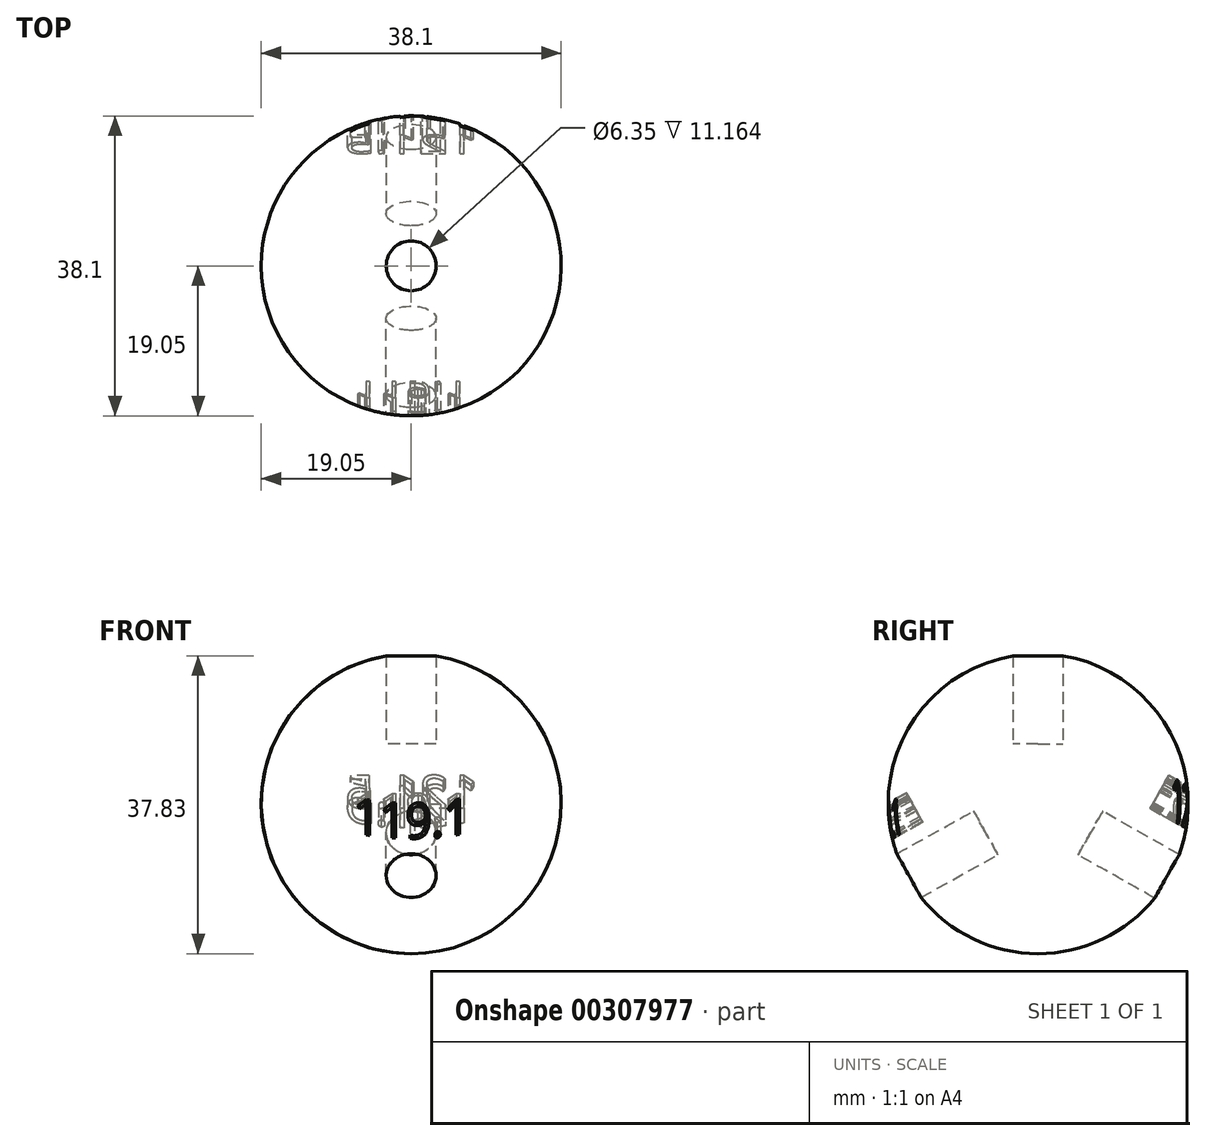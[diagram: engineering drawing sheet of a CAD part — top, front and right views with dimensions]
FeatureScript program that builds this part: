
annotation { "Feature Type Name" : "Feature", "Feature Type Description" : "" }
export const myFeature = defineFeature(function(context is Context, id is Id, definition is map)
    precondition{}
    {
        {
            var Q0;
            Q0=qCreatedBy(makeId("Front.planeOp"),FACE);
            var sketch = newSketch(context, id + "F0", { "sketchPlane" : qUnion([Q0])});
            skArc(sketch, "E0", {"start": v(0, 19.05) * mm, "mid": v(-19.05, 0) * mm, "end": v(0, -19.05) * mm});
            skLineSegment(sketch, "E1", {"start": v(0, 19.05) * mm, "end": v(0, -19.05) * mm});
            skSolve(sketch);
        }
        {
            var Q0;
            Q0=qCreatedBy(makeId("Top.planeOp"),FACE);
            var sketch = newSketch(context, id + "F1", { "sketchPlane" : qUnion([Q0])});
            skCircle(sketch, "E2", {"center": v(0, 0) * mm, "radius": 19.05 * mm});
            skSolve(sketch);
        }
        {
            var Q0;
            Q0=makeQuery(id+"F0.imprint","IMPRINT",FACE,{"disambiguationData":[TD([[makeQuery(id+"F0.imprint","IMPRINT",EDGE,{"derivedFrom":sQuery(id+"F0.wireOp",EDGE,"E0")}),1.0]])]});
            var Q1;
            Q1=sQuery(id+"F1.wireOp",EDGE,"E2");
            revolve(context, id + "F2", {"entities" : qUnion([Q0]), "axis" : qUnion([Q1]), "revolveType" : RevolveType.FULL});
        }
        {
            var Q0;
            Q0=qCreatedBy(makeId("Front.planeOp"),FACE);
            var sketch = newSketch(context, id + "F3", { "sketchPlane" : qUnion([Q0])});
            skLineSegment(sketch, "E3", {"start": v(0, 0) * mm, "end": v(76.32, 0) * mm, "construction": true});
            skLineSegment(sketch, "E4", {"start": v(0, 0) * mm, "end": v(0, 76.7) * mm, "construction": true});
            skSolve(sketch);
        }
        {
            var Q0;
            Q0=qCreatedBy(makeId("Top.planeOp"),FACE);
            cPlane(context, id + "F4", {"entities" : qUnion([Q0]), "cplaneType" : CPlaneType.OFFSET, "offset" : 7.62 * mm, "width" : 152.4 * mm, "height" : 152.4 * mm});
        }
        {
            var Q0;
            Q0=qCreatedBy(id+"F4.planeOp",FACE);
            var sketch = newSketch(context, id + "F5", { "sketchPlane" : qUnion([Q0])});
            skCircle(sketch, "E5", {"center": v(0, 0) * mm, "radius": 3.17 * mm});
            skSolve(sketch);
        }
        {
            var Q0;
            Q0=qSketchRegion(id+"F5",true);
            extrude(context, id + "F6", {"entities" : qUnion([Q0]), "depth" : 76.2 * mm});
        }
        {
            var Q0;
            Q0=makeQuery(id+"F6.opExtrude","SWEPT_BODY",BODY,{"disambiguationData":[OSD([sQuery(id+"F5.wireOp",EDGE,"E5")])]});
            var Q1;
            Q1=sQuery(id+"F3.wireOp",EDGE,"E3");
            transform(context, id + "F7", {"entities" : qUnion([Q0]), "transformType" : TransformType.ROTATION, "transformAxis" : qUnion([Q1]), "angle" : 119.1 * degree, "makeCopy" : true});
        }
        {
            var Q0;
            Q0=makeQuery(id+"F7.opPattern","COPY",BODY,{"derivedFrom":makeQuery(id+"F6.opExtrude","SWEPT_BODY",BODY,{"disambiguationData":[OSD([sQuery(id+"F5.wireOp",EDGE,"E5")])]}),"instanceName":"1"});
            var Q1;
            Q1=sQuery(id+"F3.wireOp",EDGE,"E3");
            transform(context, id + "F8", {"entities" : qUnion([Q0]), "transformType" : TransformType.ROTATION, "transformAxis" : qUnion([Q1]), "angle" : 121.5 * degree, "makeCopy" : true});
        }
        {
            var Q0;
            Q0=makeQuery(id+"F7.opPattern","COPY",FACE,{"derivedFrom":makeQuery(id+"F6.opExtrude","CAP_FACE",FACE,{"disambiguationData":[OSD([sQuery(id+"F5.wireOp",EDGE,"E5")])],"isStart":false}),"instanceName":"1"});
            cPlane(context, id + "F9", {"entities" : qUnion([Q0]), "cplaneType" : CPlaneType.OFFSET, "offset" : 63.5 * mm, "oppositeDirection" : true, "width" : 152.4 * mm, "height" : 152.4 * mm});
        }
        {
            var Q0;
            Q0=qCreatedBy(id+"F9.planeOp",FACE);
            var sketch = newSketch(context, id + "F10", { "sketchPlane" : qUnion([Q0])});
            skText(sketch, "E6", { "text": "119.1", "fontName": "OpenSans-Regular.ttf"});
            const initialGuessF10  = {"E6": [-0.00732, 0.00517, 1, 0, 0.00416]};
            skSetInitialGuess(sketch, initialGuessF10);
            skSolve(sketch);
        }
        {
            var Q0;
            Q0=qSketchRegion(id+"F10",true);
            extrude(context, id + "F11", {"entities" : qUnion([Q0]), "operationType" : NewBodyOperationType.REMOVE, "oppositeDirection" : true, "depth" : 6.35 * mm});
        }
        {
            var Q0;
            Q0=makeQuery(id+"F8.opPattern","COPY",FACE,{"derivedFrom":makeQuery(id+"F7.opPattern","COPY",FACE,{"derivedFrom":makeQuery(id+"F6.opExtrude","CAP_FACE",FACE,{"disambiguationData":[OSD([sQuery(id+"F5.wireOp",EDGE,"E5")])],"isStart":false}),"instanceName":"1"}),"instanceName":"1"});
            cPlane(context, id + "F12", {"entities" : qUnion([Q0]), "cplaneType" : CPlaneType.OFFSET, "offset" : 63.5 * mm, "oppositeDirection" : true, "width" : 152.4 * mm, "height" : 152.4 * mm});
        }
        {
            var Q0;
            Q0=qCreatedBy(id+"F12.planeOp",FACE);
            var sketch = newSketch(context, id + "F13", { "sketchPlane" : qUnion([Q0])});
            skText(sketch, "E7", { "text": "121.5\n", "fontName": "OpenSans-Regular.ttf"});
            const initialGuessF13  = {"E7": [-0.0085, 0.00654, 1, 0, 0.00478]};
            skSetInitialGuess(sketch, initialGuessF13);
            skSolve(sketch);
        }
        {
            var Q0;
            Q0=qSketchRegion(id+"F13",true);
            extrude(context, id + "F14", {"entities" : qUnion([Q0]), "operationType" : NewBodyOperationType.REMOVE, "oppositeDirection" : true, "depth" : 7.62 * mm});
        }
        {
            var Q0;
            Q0=makeQuery(id+"F6.opExtrude","SWEPT_BODY",BODY,{"disambiguationData":[OSD([sQuery(id+"F5.wireOp",EDGE,"E5")])]});
            var Q1;
            Q1=makeQuery(id+"F7.opPattern","COPY",BODY,{"derivedFrom":makeQuery(id+"F6.opExtrude","SWEPT_BODY",BODY,{"disambiguationData":[OSD([sQuery(id+"F5.wireOp",EDGE,"E5")])]}),"instanceName":"1"});
            var Q2;
            Q2=makeQuery(id+"F8.opPattern","COPY",BODY,{"derivedFrom":makeQuery(id+"F7.opPattern","COPY",BODY,{"derivedFrom":makeQuery(id+"F6.opExtrude","SWEPT_BODY",BODY,{"disambiguationData":[OSD([sQuery(id+"F5.wireOp",EDGE,"E5")])]}),"instanceName":"1"}),"instanceName":"1"});
            var Q3;
            Q3=makeQuery(id+"F2.opRevolve","SWEPT_BODY",BODY,{"disambiguationData":[OSD([sQuery(id+"F0.wireOp",EDGE,"E0"),sQuery(id+"F0.wireOp",EDGE,"E1")])]});
            booleanBodies(context, id + "F15", {"operationType" : BooleanOperationType.SUBTRACTION, "tools" : qUnion([Q0, Q1, Q2]), "targets" : qUnion([Q3])});
        }
    });
